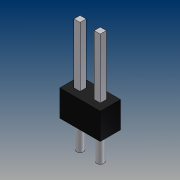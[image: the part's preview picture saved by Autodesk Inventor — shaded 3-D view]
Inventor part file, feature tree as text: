
AUTODESK INVENTOR PART (.ipt)
format: ipt  version: unknown  size: 186,880 bytes
history: native  units: mm (DEFAULTED — no unit token found)
features: extrude x3, plane x3, sketch x2, pattern_linear x1
ambient origin geometry x5: Origin, X Axis, Y Axis, Z Axis, Center Point
feature tree (9):
  extrude  "Extrusion1"  Depth=3.302mm
  sketch  "Sketch3"  dims[d2=2.54mm d3=0.0mm d4=0.762mm d5=0.889mm d6=10.795mm d7=0.0mm d8=3.429mm d9=0.0mm d10=20.0mm d12=2.54mm]
  extrude  "Extrusion2"  Depth=0.762mm
  extrude  "Extrusion3"  Depth=0.889mm
  pattern_linear  "Rectangular Pattern1"  Spacing1=10.795mm  [1 undecoded]
  plane  "YZ Plane (RIGHT)"
  plane  "XZ Plane (TOP)"
  plane  "XY Plane (FRONT)"
  sketch  "Sketch2"  dims[d0=2.54mm d1=3.302mm]
note: 1 required parameter value undecoded (feature->parameter linkage not recoverable at this tier; creation-order binding heuristic only, values carry confidence <= 0.55)
